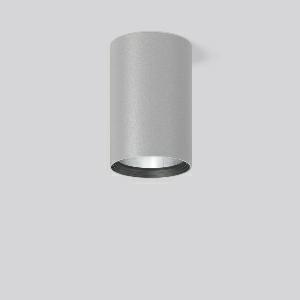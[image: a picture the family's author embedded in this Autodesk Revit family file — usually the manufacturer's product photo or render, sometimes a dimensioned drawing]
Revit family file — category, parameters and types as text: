
# Revit family: heledon_maxi_a_931226_004_1_76_fe66
name_source: partatom
category: Lighting Fixtures
units: mm (PartAtom-declared; Revit-internal decimal feet)

## family parameters
Cut with Voids When Loaded = No
Host = Face
Light Source = No
Part Type = Normal
Room Calculation Point = No
Round Connector Dimension = Use Diameter
Shared = No

## types (1)
- HELEDON maxi A (1 x LED Modul 940, 4400 lm, 4000)
    Apparent Load = 35 VA
    Approval mark = CE
    CIE Flux Codes = 97 100 100 100 100
    Color Rendering = 92
    Color Temperature = 4000
    Default Elevation = 1800 mm
    Description = Series: HELEDON maxi
Cylindrical surface-mounted downlight. Housing: die-cast aluminium, powder-coated. Internal ceiling frame polycarbonate with bayonet mounting. Black plastic ring and recessed LED to prevent glare from the side. Optical assembly with reflector made of MIRO-Silver with 98% total light reflection for outstanding efficiency - can be changed without tools. Best colour rendering index Ra>90. Suitable for Ceiling mounting. Easy installation with a separate ceiling frame with bayonet mounting and plug connection. Driver integrated. Connected via plug-in connector. High quality converter without flickering and stroboscopic effect. The following accessories can be mounted without use of tools: interchangeable lenses, decorative glasses, honeycomb louvre, clear and frosted diffusers, white interchangeable plastic ring. 
Colour: silver
Diameter: 123 mm
Height: 183 mm
Lamp: LED
Socket: without socket
Colour temperature: 4000K
Colour rendering index (CRI): 92
System power: 35 W
Rated luminous flux: 4400 lm
Luminous efficiency: 126 lm/W
Control gear: Converter, dimmable, DALI
Protection class: I
Type of protection: IP 20
    Height = 183 mm
    Lamp = 1 x LED Modul 940
    Lamp Light Flux = 4400 lm
    Lamp count = 1
    Length = 123 mm
    Lifetime = 50000 h
    Luminous efficacy = 126 lm/W
    Manufacturer = RZB
    ModVariant = No
    Model = 931226.004.1.76
    Mounting Place = Ceiling
    Mounting Type = Surface mounted
    Number of Poles = 1
    OnlyDefault = Yes
    Power Factor = 1
    Product Name = HELEDON maxi A
    Product group = Surface mounted downlights
    ProductGroupID = 302
    Protection Class = Protection class I
    Protection Degree = IP 20
    RLX_Detail_Level = 1
    RLX_Emergency_Light_Flux = 0 lm
    RLX_Emergency_Type = 0
    RLX_Emergency_Type_DB = No
    RlxData = <blob elided: 97009 chars, md5=9ee5acfb>
    Socket = socket
    Standby Power = 0 W
    System Light Flux = 4400 lm
    System Power = 35 W
    Type Comments = Product without accessories
    Type Image = 931192.004.jpg
    URL = http://relux.com
    VarID = ---
    Voltage = 230 V
    Voltage Range = 220-240 V
    Weight = 0.00 kg
    Width = 0 mm  [stored 0 ft]

note: [stored X ft] marks values corroborated as IEEE doubles in the binary element streams (Revit-internal decimal feet)

## geometry (parser evidence)
native form markers: Blend x4, Sweep x9
no freeform markers — native parametric forms only
